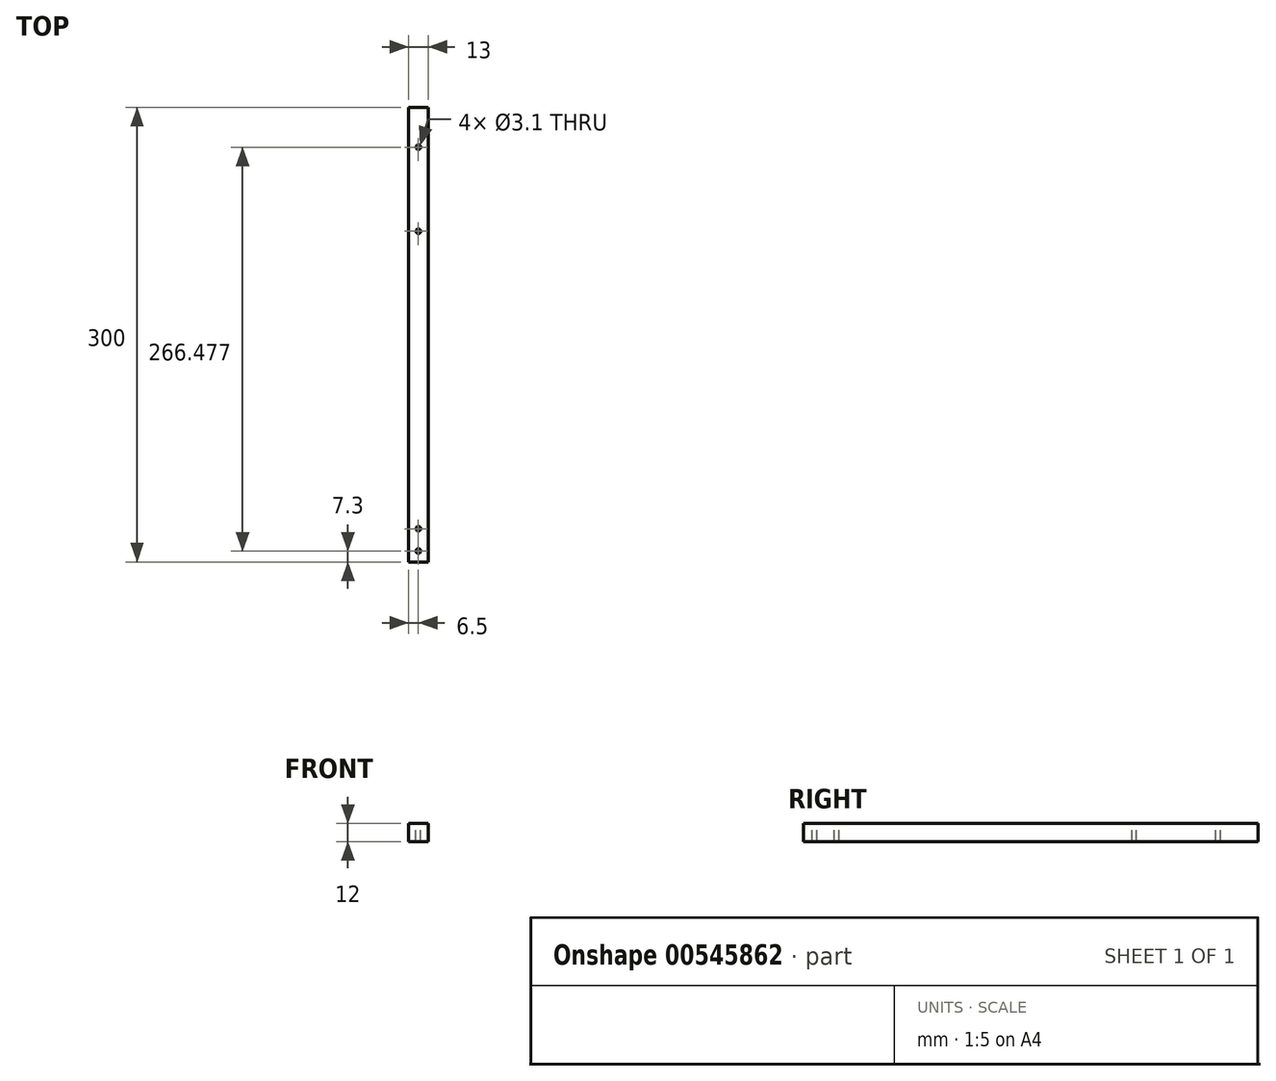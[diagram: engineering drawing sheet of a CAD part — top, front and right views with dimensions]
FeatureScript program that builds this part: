
annotation { "Feature Type Name" : "Feature", "Feature Type Description" : "" }
export const myFeature = defineFeature(function(context is Context, id is Id, definition is map)
    precondition{}
    {
        {
            var Q0;
            Q0=qCreatedBy(makeId("Front.planeOp"),FACE);
            var sketch = newSketch(context, id + "F0", { "sketchPlane" : qUnion([Q0])});
            skLineSegment(sketch, "E0.bottom", {"start": v(6.5, -6) * mm, "end": v(-6.5, -6) * mm});
            skLineSegment(sketch, "E0.top", {"start": v(6.5, 6) * mm, "end": v(-6.5, 6) * mm});
            skLineSegment(sketch, "E0.left", {"start": v(6.5, -6) * mm, "end": v(6.5, 6) * mm});
            skLineSegment(sketch, "E0.right", {"start": v(-6.5, -6) * mm, "end": v(-6.5, 6) * mm});
            skPoint(sketch, "E0.middle", {"position": v(0, 0) * mm});
            skSolve(sketch);
        }
        {
            var Q0;
            Q0=qSketchRegion(id+"F0",true);
            extrude(context, id + "F1", {"entities" : qUnion([Q0]), "oppositeDirection" : true, "depth" : 300 * mm, "offsetDistance" : 25.4 * mm});
        }
        {
            var Q0;
            Q0=makeQuery(id+"F1.opExtrude","SWEPT_FACE",FACE,{"disambiguationData":[OSD([sQuery(id+"F0.wireOp",EDGE,"E0.top")])]});
            var sketch = newSketch(context, id + "F2", { "sketchPlane" : qUnion([Q0])});
            skCircle(sketch, "E1", {"center": v(0, 7.3) * mm, "radius": 1.55 * mm});
            skCircle(sketch, "E2", {"center": v(0, 22) * mm, "radius": 1.55 * mm});
            skSolve(sketch);
        }
        {
            var Q0;
            Q0=qSketchRegion(id+"F2",true);
            extrude(context, id + "F3", {"entities" : qUnion([Q0]), "operationType" : NewBodyOperationType.REMOVE, "endBound" : BoundingType.THROUGH_ALL, "oppositeDirection" : true, "depth" : 25.4 * mm, "offsetDistance" : 25.4 * mm});
        }
        {
            var Q0;
            {var subQ0=sQuery(id+"F0.wireOp",EDGE,"E0.top");var subQ1=makeQuery(id+"F1.opExtrude","CAP_EDGE",EDGE,{"disambiguationData":[OSD([subQ0])],"isStart":false});Q0=makeQuery(id+"F2.imprint","IMPRINT",FACE,{"disambiguationData":[TD([[makeQuery(id+"F2.imprint","IMPRINT",EDGE,{"derivedFrom":subQ1}),1.0]])]});}
            var sketch = newSketch(context, id + "F4", { "sketchPlane" : qUnion([Q0])});
            skCircle(sketch, "E3", {"center": v(0, 273.78) * mm, "radius": 1.55 * mm});
            skCircle(sketch, "E4", {"center": v(0, 218.28) * mm, "radius": 1.55 * mm});
            skSolve(sketch);
        }
        {
            var Q0;
            Q0 = qSketchRegion(id + "F4", true);
            extrude(context, id + "F5", {"entities" : qUnion([Q0]), "operationType" : NewBodyOperationType.REMOVE, "oppositeDirection" : true, "depth" : 25 * mm, "offsetDistance" : 25 * mm});
        }
    });
